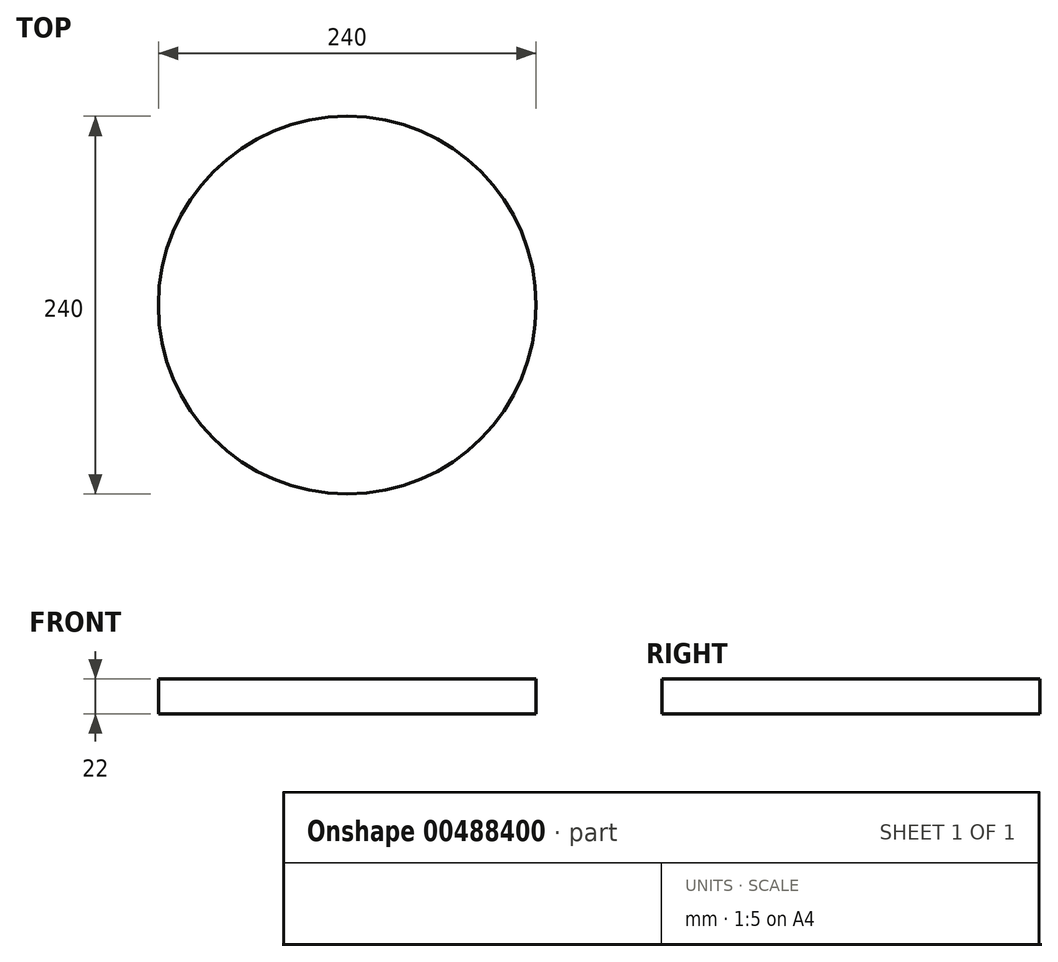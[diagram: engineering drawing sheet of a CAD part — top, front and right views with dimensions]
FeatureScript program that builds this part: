
annotation { "Feature Type Name" : "Feature", "Feature Type Description" : "" }
export const myFeature = defineFeature(function(context is Context, id is Id, definition is map)
    precondition{}
    {
        {
            var Q0;
            Q0=qCreatedBy(makeId("Top.planeOp"),FACE);
            var sketch = newSketch(context, id + "F0", { "sketchPlane" : qUnion([Q0])});
            skCircle(sketch, "E0", {"center": v(0, 0) * mm, "radius": 120 * mm});
            skSolve(sketch);
        }
        {
            var Q0;
            Q0=makeQuery(id+"F0.imprint","IMPRINT",FACE,{"disambiguationData":[TD([[makeQuery(id+"F0.imprint","IMPRINT",EDGE,{"derivedFrom":sQuery(id+"F0.wireOp",EDGE,"E0")}),1.0]])]});
            var Q1;
            Q1=makeQuery(id+"F0.imprint","IMPRINT",FACE,{"disambiguationData":[TD([[makeQuery(id+"F0.imprint","IMPRINT",EDGE,{"derivedFrom":sQuery(id+"F0.wireOp",EDGE,"iyl2Y1PO-hI79-7tgM-to39-EM1StmmzHRsz")}),1.0]])]});
            extrude(context, id + "F1", {"entities" : qUnion([Q0, Q1]), "oppositeDirection" : true, "depth" : 22 * mm});
        }
    });
